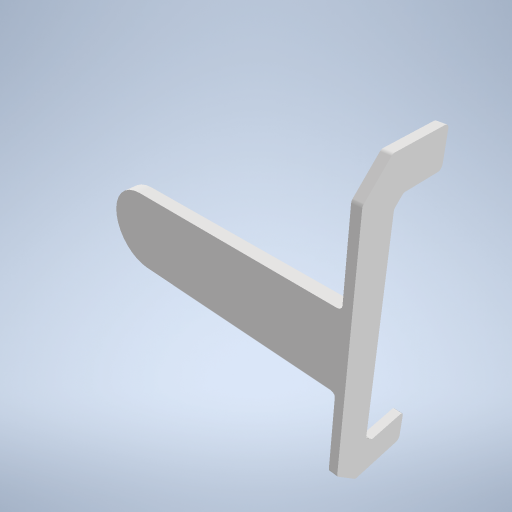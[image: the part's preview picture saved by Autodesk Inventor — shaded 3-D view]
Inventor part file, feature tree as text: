
AUTODESK INVENTOR PART (.ipt)
format: ipt  version: 2023 (Build 270158000, 158)  size: 306,176 bytes
history: native  units: in
note: dims shown in document units (in); Inventor stores cm internally (conversion verified against a paired STEP export)
features: sketch x5, extrude x4, fillet x3, chamfer x2, revolve x1
ambient origin geometry x8: Origin, YZ Plane, XZ Plane, XY Plane, X Axis, Y Axis, Z Axis, Center Point
bodies: Solid1 (feature_tree)
feature tree (15):
  extrude  "Extrusion1"  Depth=0.7087in
  extrude  "Extrusion2"  Depth=0.315in
  revolve  "Revolution1"  [1 undecoded]
  extrude  "Extrusion3"  Depth=0.3543in
  fillet  "Fillet1"  Radius=2.7559in
  extrude  "Extrusion4"  Depth=0.0787in TaperAngle=0.0deg
  chamfer  "Chamfer1"  Distance=0.7874in
  chamfer  "Chamfer2"  Distance=0.315in
  fillet  "Fillet3"  Radius=0.315in
  fillet  "Fillet4"  Radius=0.315in
  sketch  "Sketch1"  dims[d0=0.7087in d1=2.3622in]
  sketch  "Sketch2"  dims[d2=0.1181in d3=0.0in d4=0.315in]
  sketch  "Sketch4"  dims[d5=0.1969in d6=0.0in d7=0.1374in]
  sketch  "Sketch5"  dims[d8=0.0787in d9=0.0in d10=0.3543in d11=2.7559in]
  sketch  "Sketch6"  dims[d12=0.0in d13=0.0787in d14=0.0in d15=0.7874in d16=0.315in d17=0.315in d18=0.315in d19=0.7874in d21=0.2362in d22=0.0787in d23=45.0deg d24=0.0787in d25=0.0787in d26=45.0deg d27=0.0394in d28=0.0394in]
note: 1 required parameter value undecoded (feature->parameter linkage not recoverable at this tier; creation-order binding heuristic only, values carry confidence <= 0.55)
